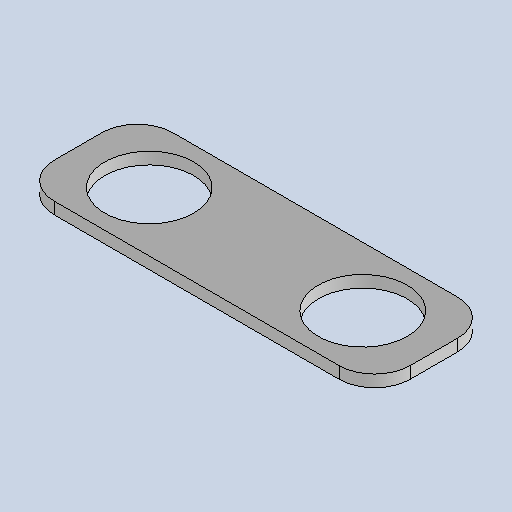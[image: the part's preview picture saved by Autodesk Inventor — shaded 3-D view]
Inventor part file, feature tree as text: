
AUTODESK INVENTOR PART (.ipt)
format: ipt  version: 2025.3 (Build 293356030, 356C)  size: 138,752 bytes
history: native  units: mm
features: other x2, sheet_metal_op x1, chamfer x1, sketch x1
ambient origin geometry x8: Origin, YZ Plane, XZ Plane, XY Plane, X Axis, Y Axis, Z Axis, Center Point
bodies: Solid1 (feature_tree)
feature tree (5):
  sheet_metal_op  "Face1"
  chamfer  "Corner Round1"
  sketch  "Sketch1"  dims[d0=60.0mm d1=20.0mm d2=15.0mm d3=36.0mm d4=2.0mm d5=6.0mm]
  other  "Plate1"
  other  "Definition1"
